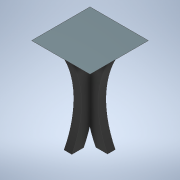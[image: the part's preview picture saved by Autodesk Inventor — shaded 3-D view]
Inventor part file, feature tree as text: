
AUTODESK INVENTOR PART (.ipt)
format: ipt  version: 2022 (Build 260153000, 153)  size: 159,232 bytes
history: native  units: mm
features: extrude x3, sketch x3, plane x2, chamfer x1, direct_edit x1, other x1
ambient origin geometry x8: Origin, YZ Plane, XZ Plane, XY Plane, X Axis, Y Axis, Z Axis, Center Point
bodies: Solid1 (feature_tree)
feature tree (11):
  extrude  "Extrusion1"  Depth=7.5mm
  plane  "Work Plane1"
  plane  "Work Plane2"
  chamfer  "Chamfer1"  Distance=1.0mm
  extrude  "Extrusion2"  Depth=10.0mm
  extrude  "Extrusion3"  Depth=10.0mm
  direct_edit  "Direct Edit1"
  sketch  "Sketch1"  dims[d0=7.5mm d1=7.5mm]
  sketch  "Sketch2"  dims[d2=0.0mm d3=1.0mm d4=0.0mm]
  sketch  "Sketch3"  dims[d5=1.0mm d6=2.0mm d7=45.0deg d8=1.5mm d9=10.0mm d10=0.0mm d11=11.0mm d12=11.0mm d13=14.79686mm d14=1.0mm d15=0.0mm d16=1.5mm d17=1.5mm d18=0.0mm d19=10.0mm d20=0.0mm d21=11.0mm d22=11.0mm d23=1.0mm d24=0.0mm d25=20.0mm d26=10.0mm d27=10.0mm]
  other  "Scale1"
